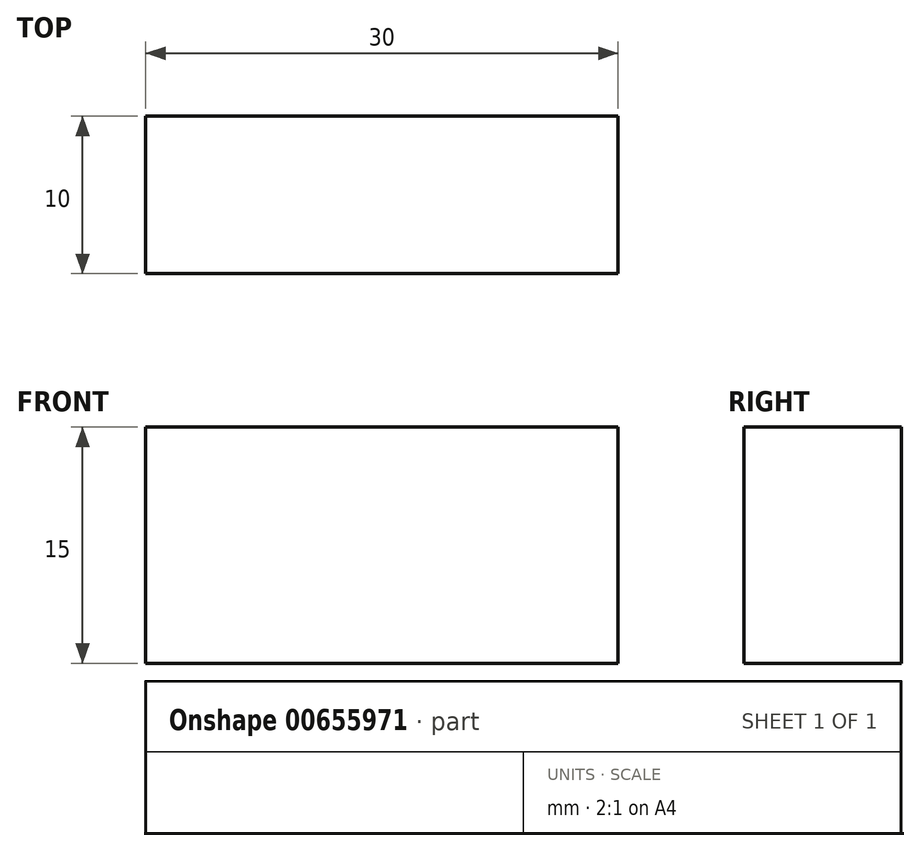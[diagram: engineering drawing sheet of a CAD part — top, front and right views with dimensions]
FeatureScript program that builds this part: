
annotation { "Feature Type Name" : "Feature", "Feature Type Description" : "" }
export const myFeature = defineFeature(function(context is Context, id is Id, definition is map)
    precondition{}
    {
        {
            var Q0;
            Q0=qCreatedBy(makeId("Top.planeOp"),FACE);
            var sketch = newSketch(context, id + "F0", { "sketchPlane" : qUnion([Q0])});
            skLineSegment(sketch, "E0.bottom", {"start": v(0, 0) * mm, "end": v(-30, 0) * mm});
            skLineSegment(sketch, "E0.top", {"start": v(0, -10) * mm, "end": v(-30, -10) * mm});
            skLineSegment(sketch, "E0.left", {"start": v(0, 0) * mm, "end": v(0, -10) * mm});
            skLineSegment(sketch, "E0.right", {"start": v(-30, 0) * mm, "end": v(-30, -10) * mm});
            skSolve(sketch);
        }
        {
            var Q0;
            Q0 = qSketchRegion(id + "F0", true);
            extrude(context, id + "F1", {"entities" : qUnion([Q0]), "depth" : 15 * mm, "offsetDistance" : 25 * mm});
        }
    });
